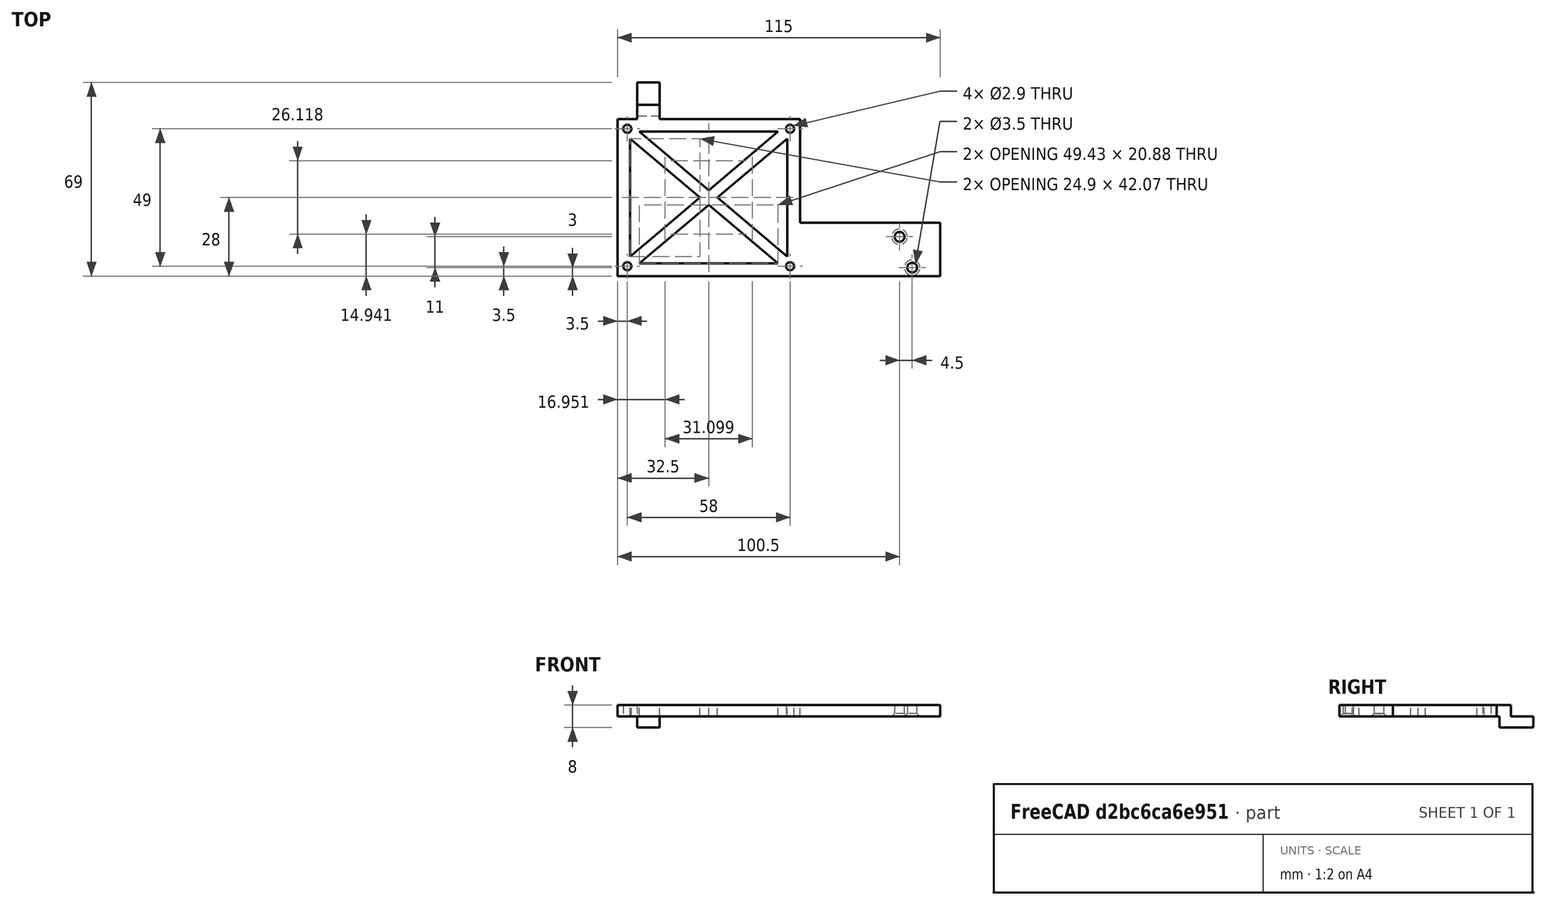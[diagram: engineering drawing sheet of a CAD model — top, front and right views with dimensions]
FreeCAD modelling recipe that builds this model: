
FCSTD DOCUMENT  (FreeCAD 0.18R16146 (Git))
Label: pi4OverMotorMount
License: All rights reserved
LicenseURL: http://en.wikipedia.org/wiki/All_rights_reserved
objects: Sketcher::SketchObject×6, PartDesign::Pad×5, PartDesign::Pocket×2, PartDesign::Chamfer×1, PartDesign::Body×1
note: 22 computed .brp shape members not serialized (recipe doc carries the construction recipe); baked Part::Feature solids carry a one-line shape summary decoded from their .brp

FEATURE [Sketcher::SketchObject] Sketch
  MapMode = 5
  Support = -> [XY_Plane]
  sketch-geometry (30):
    g0: LineSegment StartX=1.7e-15 StartY=56 StartZ=0 EndX=65 EndY=56 EndZ=0
    g1: LineSegment StartX=65 StartY=56 StartZ=0 EndX=65 EndY=0 EndZ=0
    g2: LineSegment StartX=65 StartY=0 StartZ=0 EndX=0 EndY=0 EndZ=0
    g3: LineSegment StartX=0 StartY=0 StartZ=0 EndX=1.7e-15 EndY=56 EndZ=0
    g4: LineSegment [constr] StartX=3.5 StartY=52.5 StartZ=0 EndX=61.5 EndY=52.5 EndZ=0
    g5: LineSegment [constr] StartX=61.5 StartY=52.5 StartZ=0 EndX=61.5 EndY=3.5 EndZ=0
    g6: LineSegment [constr] StartX=61.5 StartY=3.5 StartZ=0 EndX=3.5 EndY=3.5 EndZ=0
    g7: LineSegment [constr] StartX=3.5 StartY=3.5 StartZ=0 EndX=3.5 EndY=52.5 EndZ=0
    g8: LineSegment StartX=7.78276 StartY=51.5 StartZ=0 EndX=57.2172 EndY=51.5 EndZ=0
    g9: LineSegment StartX=60.5 StartY=49.037 StartZ=0 EndX=60.5 EndY=6.96302 EndZ=0
    g10: LineSegment StartX=57.2172 StartY=4.5 StartZ=0 EndX=7.78276 EndY=4.5 EndZ=0
    g11: LineSegment StartX=4.5 StartY=6.96302 StartZ=0 EndX=4.5 EndY=49.037 EndZ=0
    g12: LineSegment [constr] StartX=3.5 StartY=52.5 StartZ=0 EndX=61.5 EndY=3.5 EndZ=0
    g13: LineSegment [constr] StartX=3.5 StartY=3.5 StartZ=0 EndX=61.5 EndY=52.5 EndZ=0
    g14: LineSegment [constr] StartX=32.5 StartY=28 StartZ=0 EndX=32.5 EndY=51.5 EndZ=0
    g15: LineSegment StartX=7.78276 StartY=51.5 StartZ=0 EndX=32.5 EndY=30.6182 EndZ=0
    g16: LineSegment StartX=32.5 StartY=30.6182 StartZ=0 EndX=57.2172 EndY=51.5 EndZ=0
    g17: LineSegment [constr] StartX=32.5 StartY=28 StartZ=0 EndX=4.5 EndY=28 EndZ=0
    g18: LineSegment [constr] StartX=32.5 StartY=28 StartZ=0 EndX=32.5 EndY=4.5 EndZ=0
    g19: LineSegment [constr] StartX=32.5 StartY=28 StartZ=0 EndX=60.5 EndY=28 EndZ=0
    g20: LineSegment StartX=4.5 StartY=49.037 StartZ=0 EndX=29.4009 EndY=28 EndZ=0
    g21: LineSegment StartX=29.4009 StartY=28 StartZ=0 EndX=4.5 EndY=6.96302 EndZ=0
    g22: LineSegment StartX=35.5991 StartY=28 StartZ=0 EndX=60.5 EndY=49.037 EndZ=0
    g23: LineSegment StartX=32.5 StartY=25.3818 StartZ=0 EndX=7.78276 EndY=4.5 EndZ=0
    g24: LineSegment StartX=32.5 StartY=25.3818 StartZ=0 EndX=57.2172 EndY=4.5 EndZ=0
    g25: LineSegment StartX=35.5991 StartY=28 StartZ=0 EndX=60.5 EndY=6.96302 EndZ=0
    g26: Circle CenterX=3.5 CenterY=52.5 CenterZ=0 NormalX=0 NormalY=0 NormalZ=1 AngleXU=0 Radius=1.45
    g27: Circle CenterX=61.5 CenterY=52.5 CenterZ=0 NormalX=0 NormalY=0 NormalZ=1 AngleXU=0 Radius=1.45
    g28: Circle CenterX=3.5 CenterY=3.5 CenterZ=0 NormalX=0 NormalY=0 NormalZ=1 AngleXU=0 Radius=1.45
    g29: Circle CenterX=61.5 CenterY=3.5 CenterZ=0 NormalX=0 NormalY=0 NormalZ=1 AngleXU=0 Radius=1.45
  constraints (84):
    c: Coincident(g0,g1)
    c: Coincident(g3,g0)
    c: Horizontal(g0)
    c: Horizontal(g2)
    c: Vertical(g1)
    c: Distance(g0) = 65
    c: Coincident(g4,g5)
    c: Coincident(g5,g6)
    c: Coincident(g6,g7)
    c: Coincident(g7,g4)
    c: Horizontal(g4)
    c: Horizontal(g6)
    c: Vertical(g5)
    c: Vertical(g7)
    c: Distance(g4) = 58
    c: Distance(g5) = 49
    c: Distance(g4,g3) = 3.5
    c: Horizontal(g8)
    c: Horizontal(g10)
    c: Vertical(g9)
    c: Vertical(g11)
    c: PointOnObject(g14,g13)
    c: PointOnObject(g14,g8)
    c: Vertical(g14)
    c: Distance(g4,g0) = 3.5
    c: PointOnObject(g14,g12)
    c: PointOnObject(g15,g14)
    c: Parallel(g15,g12)
    c: Distance(g15,g12) = 2
    c: Coincident(g16,g15)
    c: Parallel(g16,g13)
    c: Coincident(g17,g14)
    c: PointOnObject(g17,g11)
    c: Horizontal(g17)
    c: PointOnObject(g18,g10)
    c: Vertical(g18)
    c: Coincident(g18,g14)
    c: PointOnObject(g19,g9)
    c: Horizontal(g19)
    c: Coincident(g19,g14)
    c: PointOnObject(g20,g17)
    c: Parallel(g20,g12)
    c: Distance(g20,g12) = 2
    c: Coincident(g21,g20)
    c: Parallel(g21,g13)
    c: Parallel(g23,g13)
    c: PointOnObject(g23,g18)
    c: Distance(g23,g13) = 2
    c: Parallel(g22,g13)
    c: PointOnObject(g22,g19)
    c: Distance(g22,g13) = 2
    c: Coincident(g24,g23)
    c: Coincident(g25,g22)
    c: Parallel(g25,g12)
    c: Parallel(g24,g12)
    c: Coincident(g8,g15)
    c: Coincident(g11,g20)
    c: Distance(g8,g4) = 1
    c: Coincident(g8,g16)
    c: Coincident(g9,g22)
    c: Coincident(g10,g24)
    c: Coincident(g9,g25)
    c: Coincident(g10,g23)
    c: Coincident(g11,g21)
    c: Coincident(g13,g4)
    c: Coincident(g13,g6)
    c: Coincident(g12,g5)
    c: Distance(g10,g6) = 1
    c: Coincident(g12,g4)
    c: Distance(g11,g7) = 1
    c: Distance(g9,g5) = 1
    c: Coincident(g26,g4)
    c: Radius(g26) = 1.45
    c: Equal(g26,g27) = 1.25
    c: Coincident(g27,g4)
    c: Equal(g26,g28) = 1.25
    c: Coincident(g28,g6)
    c: Equal(g26,g29) = 1.25
    c: Coincident(g29,g5)
    c: Distance(g29,g2) = 3.5
    c: Coincident(g1,g2)
    c: Equal(g0,g2)
    c: Coincident(g3,g2)
    c: Coincident(g2,g-1)
FEATURE [PartDesign::Pad] Pad
  Length = 4
  Length2 = 100
  Profile = -> Sketch
  Type = 0
FEATURE [Sketcher::SketchObject] Sketch002
  MapMode = 5
  Placement = pos=(-1.55844,1.84468,0) rot=(-0.250463,0.684569,0.684569;3.63242rad)
  sketch-geometry (5):
    g0: Circle CenterX=-21.5 CenterY=5.25 CenterZ=0 NormalX=0 NormalY=0 NormalZ=1 AngleXU=0 Radius=1.25
    g1: LineSegment [constr] StartX=-21.5 StartY=5.25 StartZ=0 EndX=-4.5 EndY=5.25 EndZ=0
    g2: LineSegment [constr] StartX=-13 StartY=8 StartZ=0 EndX=-13 EndY=0 EndZ=0
    g3: Circle CenterX=-4.5 CenterY=5.25 CenterZ=0 NormalX=0 NormalY=0 NormalZ=1 AngleXU=0 Radius=1.25
    g4: LineSegment [constr] StartX=-21.5 StartY=5.25 StartZ=0 EndX=-21.5 EndY=4 EndZ=0
  constraints (10):
    c: Radius(g0) = 1.25
    c: Coincident(g1,g0)
    c: Distance(g1) = 17
    c: PointOnObject(g2,g-1)
    c: Symmetric(g0,g1,g2)
    c: Equal(g0,g3) = 1.25
    c: Coincident(g3,g1)
    c: Coincident(g4,g0)
    c: PointOnObject(g4,g0)
    c: Vertical(g4)
FEATURE [PartDesign::Pocket] Pocket
  BaseFeature = -> Pad
  Length = 5
  Length2 = 100
  Profile = -> Sketch002
  Type = 0
FEATURE [Sketcher::SketchObject] Sketch005
  MapMode = 5
  Placement = pos=(65,0,0) rot=(0.57735,0.57735,0.57735;2.0944rad)
  sketch-geometry (4):
    g0: LineSegment StartX=0 StartY=0 StartZ=0 EndX=19 EndY=0 EndZ=0
    g1: LineSegment StartX=19 StartY=0 StartZ=0 EndX=19 EndY=4 EndZ=0
    g2: LineSegment StartX=19 StartY=4 StartZ=0 EndX=0 EndY=4 EndZ=0
    g3: LineSegment StartX=0 StartY=4 StartZ=0 EndX=0 EndY=0 EndZ=0
  constraints (10):
    c: Coincident(g0,g1)
    c: Coincident(g1,g2)
    c: Coincident(g2,g3)
    c: Coincident(g3,g0)
    c: Horizontal(g0)
    c: Horizontal(g2)
    c: Vertical(g1)
    c: Vertical(g3)
    c: Coincident(g0,g-1)
    c: Distance(g2) = 19
FEATURE [PartDesign::Pad] Pad002
  BaseFeature = -> Pocket
  Length = 50
  Length2 = 100
  Profile = -> Sketch005
  Type = 0
FEATURE [Sketcher::SketchObject] Sketch006
  ExternalGeometry = -> [Pad002]
  MapMode = 5
  Placement = pos=(0,56,0) rot=(0,0.707107,0.707107;3.14159rad)
  Support = -> [Pad002]
  sketch-geometry (4):
    g0: LineSegment StartX=-7 StartY=0 StartZ=0 EndX=-15 EndY=0 EndZ=0
    g1: LineSegment StartX=-15 StartY=0 StartZ=0 EndX=-15 EndY=4 EndZ=0
    g2: LineSegment StartX=-15 StartY=4 StartZ=0 EndX=-7 EndY=4 EndZ=0
    g3: LineSegment StartX=-7 StartY=4 StartZ=0 EndX=-7 EndY=0 EndZ=0
  constraints (12):
    c: Coincident(g0,g1)
    c: Coincident(g1,g2)
    c: Coincident(g2,g3)
    c: Coincident(g3,g0)
    c: Horizontal(g0)
    c: Horizontal(g2)
    c: Vertical(g1)
    c: Vertical(g3)
    c: PointOnObject(g1,g-3)
    c: Distance(g2) = 8
    c: PointOnObject(g0,g-1)
    c: Distance(g-3,g3) = 7
FEATURE [PartDesign::Pad] Pad003
  BaseFeature = -> Pad002
  Length = 5
  Length2 = 100
  Profile = -> Sketch006
  Type = 0
FEATURE [Sketcher::SketchObject] Sketch007
  ExternalGeometry = -> [Pad003]
  MapMode = 5
  Placement = pos=(0,0,1.24e-14) rot=(1,0,0;3.14159rad)
  Support = -> [Pad003]
  sketch-geometry (4):
    g0: LineSegment StartX=7 StartY=-61 StartZ=0 EndX=15 EndY=-61 EndZ=0
    g1: LineSegment StartX=15 StartY=-61 StartZ=0 EndX=15 EndY=-57 EndZ=0
    g2: LineSegment StartX=15 StartY=-57 StartZ=0 EndX=7 EndY=-57 EndZ=0
    g3: LineSegment StartX=7 StartY=-57 StartZ=0 EndX=7 EndY=-61 EndZ=0
  constraints (10):
    c: Coincident(g0,g1)
    c: Coincident(g1,g2)
    c: Coincident(g2,g3)
    c: Coincident(g3,g0)
    c: Horizontal(g2)
    c: Vertical(g1)
    c: Vertical(g3)
    c: Distance(g3) = 4
    c: Coincident(g0,g-6)
    c: Coincident(g0,g-6)
FEATURE [PartDesign::Pad] Pad004
  BaseFeature = -> Pad003
  Length = 4
  Length2 = 100
  Profile = -> Sketch007
  Type = 0
FEATURE [PartDesign::Pad] Pad005
  BaseFeature = -> Pad004
  Length = 8
  Length2 = 100
  Profile = -> Pad004 [Face36]
  Type = 0
FEATURE [Sketcher::SketchObject] Sketch008
  MapMode = 5
  Placement = pos=(0,0,0) rot=(1,0,0;3.14159rad)
  Support = -> [Pad005]
  sketch-geometry (2):
    g0: Circle CenterX=105 CenterY=-3 CenterZ=0 NormalX=0 NormalY=0 NormalZ=1 AngleXU=0 Radius=1.75
    g1: Circle CenterX=100.5 CenterY=-14 CenterZ=0 NormalX=0 NormalY=0 NormalZ=1 AngleXU=0 Radius=1.75
  constraints (6):
    c: Radius(g0) = 1.75
    c: Equal(g0,g1)
    c: DistanceY(g-1,g0) = -3
    c: DistanceY(g-1,g1) = -14
    c: DistanceX(g-2,g0) = 105
    c: DistanceX(g-2,g1) = 100.5
FEATURE [PartDesign::Pocket] Pocket001
  BaseFeature = -> Pad005
  Length = 5
  Length2 = 100
  Profile = -> Sketch008
  Type = 1
FEATURE [PartDesign::Chamfer] Chamfer
  Base = -> Pocket001 [Edge69,Edge70]
  BaseFeature = -> Pocket001
  Size = 1
FEATURE [PartDesign::Body] Body
  Group = -> [Sketch,Pad,Sketch002,Pocket,Sketch005,Pad002,Sketch006,Pad003,Sketch007,Pad004,Pad005,Sketch008,Pocket001,Chamfer]
  Origin = -> Origin
  Tip = -> Chamfer
